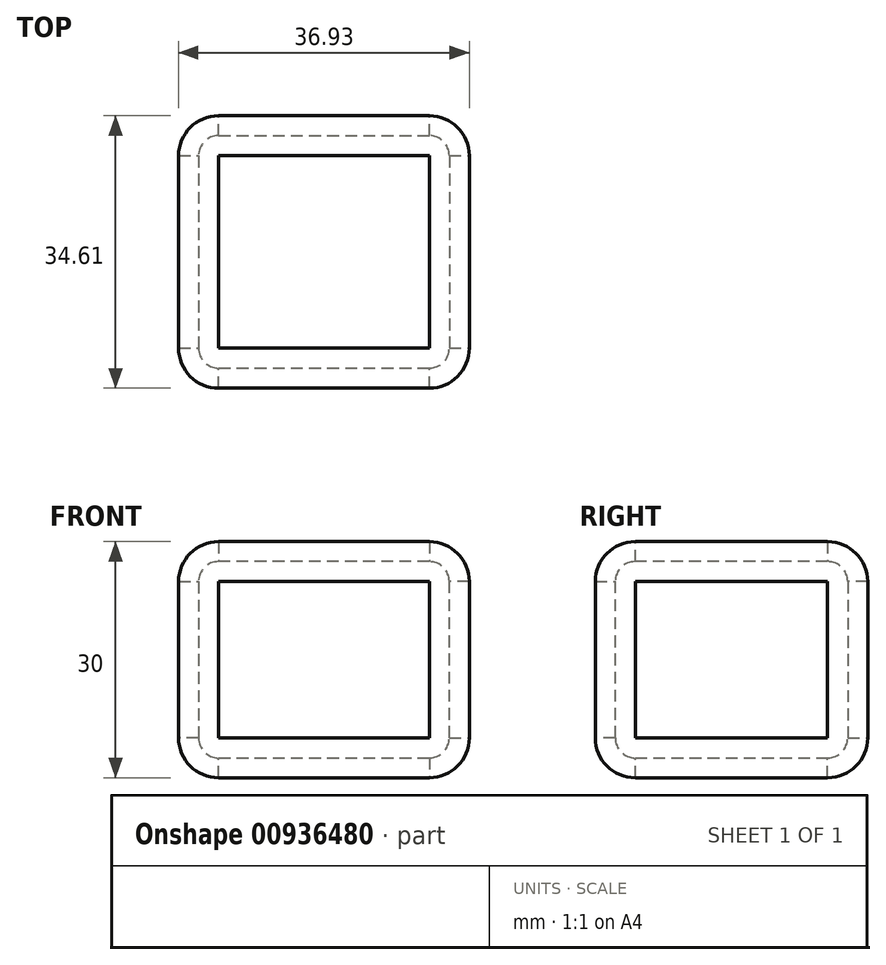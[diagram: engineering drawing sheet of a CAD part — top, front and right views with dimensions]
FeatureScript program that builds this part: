
annotation { "Feature Type Name" : "Feature", "Feature Type Description" : "" }
export const myFeature = defineFeature(function(context is Context, id is Id, definition is map)
    precondition{}
    {
        {
            var Q0;
            Q0=qCreatedBy(makeId("Top.planeOp"),FACE);
            var sketch = newSketch(context, id + "F0", { "sketchPlane" : qUnion([Q0])});
            skLineSegment(sketch, "E0.bottom", {"start": v(0, 0) * mm, "end": v(36.93, 0) * mm});
            skLineSegment(sketch, "E0.top", {"start": v(0, -34.61) * mm, "end": v(36.93, -34.61) * mm});
            skLineSegment(sketch, "E0.left", {"start": v(0, 0) * mm, "end": v(0, -34.61) * mm});
            skLineSegment(sketch, "E0.right", {"start": v(36.93, 0) * mm, "end": v(36.93, -34.61) * mm});
            skSolve(sketch);
        }
        {
            var Q0;
            Q0 = qSketchRegion(id + "F0", true);
            extrude(context, id + "F1", {"entities" : qUnion([Q0]), "depth" : 30 * mm, "offsetDistance" : 25.4 * mm});
        }
        {
            var Q0;
            Q0=makeQuery(id+"F1.opExtrude","SWEPT_EDGE",EDGE,{"disambiguationData":[OSD([sQuery(id+"F0.wireOp",EDGE,"E0.top"),sQuery(id+"F0.wireOp",EDGE,"E0.right")])]});
            var Q1;
            Q1=makeQuery(id+"F1.opExtrude","SWEPT_EDGE",EDGE,{"disambiguationData":[OSD([sQuery(id+"F0.wireOp",EDGE,"E0.bottom"),sQuery(id+"F0.wireOp",EDGE,"E0.right")])]});
            var Q2;
            Q2=makeQuery(id+"F1.opExtrude","CAP_EDGE",EDGE,{"disambiguationData":[OSD([sQuery(id+"F0.wireOp",EDGE,"E0.right")])],"isStart":true});
            var Q3;
            Q3=makeQuery(id+"F1.opExtrude","CAP_EDGE",EDGE,{"disambiguationData":[OSD([sQuery(id+"F0.wireOp",EDGE,"E0.top")])],"isStart":true});
            var Q4;
            Q4=makeQuery(id+"F1.opExtrude","CAP_EDGE",EDGE,{"disambiguationData":[OSD([sQuery(id+"F0.wireOp",EDGE,"E0.left")])],"isStart":true});
            var Q5;
            Q5=makeQuery(id+"F1.opExtrude","CAP_EDGE",EDGE,{"disambiguationData":[OSD([sQuery(id+"F0.wireOp",EDGE,"E0.bottom")])],"isStart":true});
            var Q6;
            Q6=makeQuery(id+"F1.opExtrude","CAP_EDGE",EDGE,{"disambiguationData":[OSD([sQuery(id+"F0.wireOp",EDGE,"E0.bottom")])],"isStart":false});
            var Q7;
            Q7=makeQuery(id+"F1.opExtrude","CAP_EDGE",EDGE,{"disambiguationData":[OSD([sQuery(id+"F0.wireOp",EDGE,"E0.right")])],"isStart":false});
            var Q8;
            Q8=makeQuery(id+"F1.opExtrude","CAP_EDGE",EDGE,{"disambiguationData":[OSD([sQuery(id+"F0.wireOp",EDGE,"E0.top")])],"isStart":false});
            var Q9;
            Q9=makeQuery(id+"F1.opExtrude","SWEPT_EDGE",EDGE,{"disambiguationData":[OSD([sQuery(id+"F0.wireOp",EDGE,"E0.top"),sQuery(id+"F0.wireOp",EDGE,"E0.left")])]});
            var Q10;
            Q10=makeQuery(id+"F1.opExtrude","CAP_EDGE",EDGE,{"disambiguationData":[OSD([sQuery(id+"F0.wireOp",EDGE,"E0.left")])],"isStart":false});
            var Q11;
            Q11=makeQuery(id+"F1.opExtrude","SWEPT_EDGE",EDGE,{"disambiguationData":[OSD([sQuery(id+"F0.wireOp",EDGE,"E0.bottom"),sQuery(id+"F0.wireOp",EDGE,"E0.left")])]});
            fillet(context, id + "F2", {"entities" : qUnion([Q0, Q1, Q2, Q3, Q4, Q5, Q6, Q7, Q8, Q9, Q10, Q11]), "radius" : 5.08 * mm, "tangentPropagation" : true, "allowEdgeOverflow" : false});
        }
        {
            var Q0;
            Q0=makeQuery(id+"F1.opExtrude","CAP_FACE",FACE,{"disambiguationData":[OSD([sQuery(id+"F0.wireOp",EDGE,"E0.bottom"),sQuery(id+"F0.wireOp",EDGE,"E0.top"),sQuery(id+"F0.wireOp",EDGE,"E0.left"),sQuery(id+"F0.wireOp",EDGE,"E0.right")])],"isStart":false});
            var Q1;
            Q1=makeQuery(id+"F1.opExtrude","SWEPT_FACE",FACE,{"disambiguationData":[OSD([sQuery(id+"F0.wireOp",EDGE,"E0.top")])]});
            var Q2;
            Q2=makeQuery(id+"F1.opExtrude","SWEPT_FACE",FACE,{"disambiguationData":[OSD([sQuery(id+"F0.wireOp",EDGE,"E0.bottom")])]});
            var Q3;
            Q3=makeQuery(id+"F1.opExtrude","SWEPT_FACE",FACE,{"disambiguationData":[OSD([sQuery(id+"F0.wireOp",EDGE,"E0.left")])]});
            var Q4;
            Q4=makeQuery(id+"F1.opExtrude","CAP_FACE",FACE,{"disambiguationData":[OSD([sQuery(id+"F0.wireOp",EDGE,"E0.bottom"),sQuery(id+"F0.wireOp",EDGE,"E0.top"),sQuery(id+"F0.wireOp",EDGE,"E0.left"),sQuery(id+"F0.wireOp",EDGE,"E0.right")])],"isStart":true});
            var Q5;
            Q5=makeQuery(id+"F1.opExtrude","SWEPT_FACE",FACE,{"disambiguationData":[OSD([sQuery(id+"F0.wireOp",EDGE,"E0.right")])]});
            shell(context, id + "F3", {"entities" : qUnion([Q0, Q1, Q2, Q3, Q4, Q5]), "thickness" : 2.54 * mm});
        }
    });
